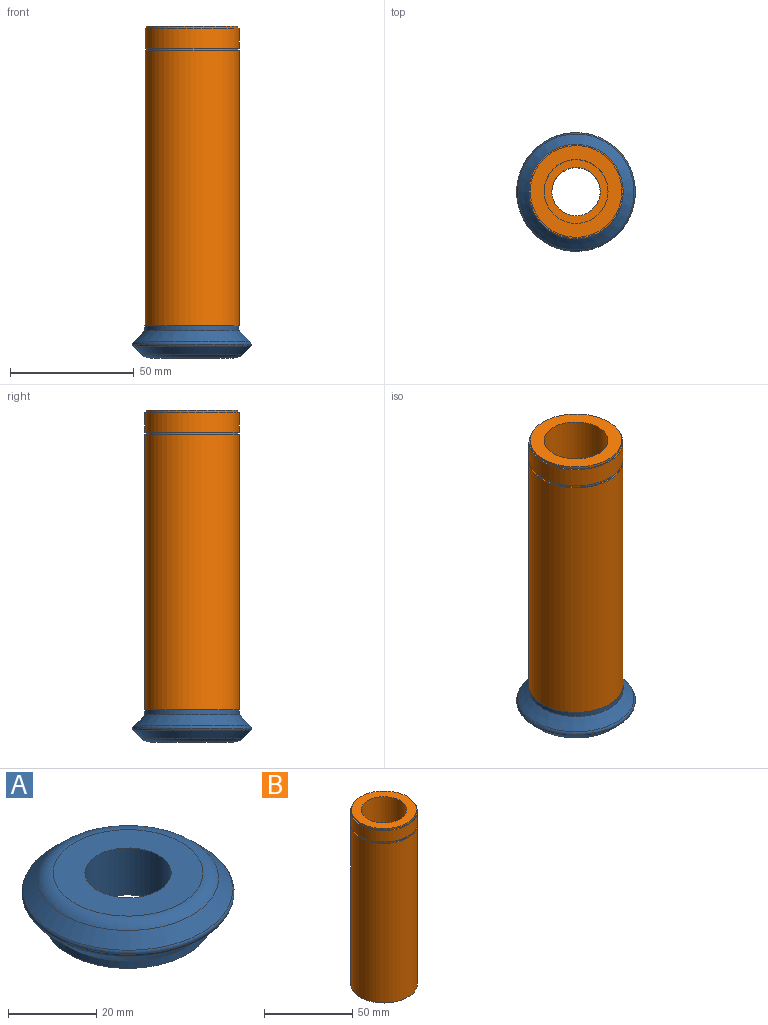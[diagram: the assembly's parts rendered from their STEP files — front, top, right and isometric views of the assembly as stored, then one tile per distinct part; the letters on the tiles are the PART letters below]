
ASSEMBLY  parts=2 mates=1
PART A: 9 faces, bbox 52x52x13 mm
  f0: cylinder r=19mm len=38mm, axis (0,0,-1), area 238.8mm2, adj f1,f5
  f1: plane 38x38mm, normal (0,0,-1), area 835.5mm2, adj f0,f3
  f2: plane 33.86x33.86mm, normal (0,0,1), area 601.7mm2, adj f3,f8
  f3: cylinder r=9.75mm len=19.5mm, axis (0,0,1), area 796.4mm2, adj f1,f2
  f4: cone r=19mm half-angle=45deg, axis (0,0,-1), area 631.3mm2, adj f7,f8
  f5: cone r=24mm half-angle=45deg, axis (0,0,1), area 831.8mm2, adj f0,f6
  f6: torus R=22mm, axis (0,0,-1), area 168.5mm2, adj f5,f7
  f7: torus R=22.98mm, axis (0,0,1), area 151mm2, adj f4,f6
  f8: torus R=16.93mm, axis (0,0,1), area 463.7mm2, adj f2,f4
PART B: 12 faces, bbox 38x38x121 mm
  f0: cylinder r=9.75mm len=66mm, axis (0,0,1), area 4043.2mm2, adj f3,f11
  f1: cylinder r=19mm len=111mm, axis (0,0,-1), area 13251.2mm2, adj f2,f3
  f2: plane 38x38mm, normal (0,0,1), area 58.9mm2, adj f1,f4
  f3: plane 38x38mm, normal (0,0,-1), area 835.5mm2, adj f0,f1
  f4: cylinder r=18.5mm len=37mm, axis (0,0,-1), area 116.2mm2, adj f2,f7
  f5: cylinder r=19mm len=38mm, axis (0,0,-1), area 955mm2, adj f6,f7
  f6: plane 38x38mm, normal (0,0,1), area 58.9mm2, adj f5,f8
  f7: plane 38x38mm, normal (0,0,-1), area 58.9mm2, adj f4,f5
  f8: cylinder r=18.5mm len=37mm, axis (0,0,-1), area 116.2mm2, adj f6,f9
  f9: plane 37x37mm, normal (0,0,1), area 552.4mm2, adj f8,f10
  f10: cylinder r=12.9mm len=55mm, axis (0,0,1), area 4457.9mm2, adj f9,f11
  f11: plane 25.8x25.8mm, normal (0,0,1), area 224.1mm2, adj f0,f10
PLACE A rot(axis=(0,1,0),180deg) t=(-65.4,-1.47,-6.06)mm
PLACE B t=(-65.4,-1.47,-6.06)mm
MATE fastened A.f0 <-> B.f1  axis (0,0,1) through (-65.4,-1.47,-6.06)mm
